# Revit family: KEUCO_14975010000
name_source: partatom
category: Allgemeines Modell
revit_build: Autodesk Revit 2016 (Build: 20150220_1215(x64)
units: mm (PartAtom-declared; Revit-internal decimal feet)

## family parameters
Arbeitsebenenbasiert = Ja
Beim Laden mit Abzugskörper schneiden = Nein
Bemaßung runder Anschluss = Durchmesser verwenden
Gemeinsam genutzt = Nein
Immer vertikal = Nein
Kann Basisbauteil für Bewehrung sein = Nein
Raumberechnungspunkt = Nein
Teiletyp = Normal

## types (3) — shared parameters
Beschreibung = mit Ablage aus ESG-Glas
Gewicht = 1.46
Hersteller = KEUCO
Kategorie = ACC
Länge = 600 mm  [stored 1.9685 ft]
Material Regal = Glas, weiß, hohe Luminanz
Serie = Plan
Tiefe = 235 mm  [stored 0.770997 ft]
URL = https://www.keuco.com
Verwendung = GWC / WP
Vorgabe-Ansicht = 1219 mm

## per-type parameters (varying)
| type | Ausschreibungstext | Rahmen Material |
| 14975010000 | KEUCO PLAN Handtuchablage, 14975010000
Handtuchablage aus transparentem ESG, Stärke 8 mm, 
Gesamtbreite 600 mm,
in ästhetischem, funktionalem Design, 
Handtuchhalter aus hochglanzverchromten Messingrohr, 
Durchmesser 25 mm,
leicht zu reinigen, antistatisch, Ausladung Handtuchhalter 112 mm,
Gesamthöhe 112 mm, Gesamtbreite 600 mm, Ausladung 235 mm,
die Handtuchablage wird verdeckt angebracht,
Lieferung inkl. korrosionsfreiem Befestigungsmaterial | Verchromt |
| 14975070000 | KEUCO PLAN Handtuchablage, 14975070000
Handtuchablage aus transparentem ESG, Stärke 8 mm, 
Gesamtbreite 600 mm,
in ästhetischem, funktionalem Design, 
Handtuchhalter aus hochwertigem Edelstahl, 
Durchmesser 25 mm,
leicht zu reinigen, antistatisch, Ausladung Handtuchhalter 112 mm,
Gesamthöhe 112 mm, Gesamtbreite 600 mm, Ausladung 235 mm,
die Handtuchablage wird verdeckt angebracht,
Lieferung inkl. korrosionsfreiem Befestigungsmaterial | Edelstahl |
| 14975170000 | KEUCO PLAN Handtuchablage, 14975170000
Handtuchablage aus transparentem ESG, Stärke 8 mm, 
Gesamtbreite 600 mm,
in ästhetischem, funktionalem Design, 
Handtuchhalter aus silber-exloxiertem Aluminiumrohr, 
Durchmesser 25 mm,
die Glasaufnahmen sind als Design-Element hochglanzverchromt,
leicht zu reinigen, antistatisch, Ausladung Handtuchhalter 112 mm,
Gesamthöhe 112 mm, Gesamtbreite 600 mm, Ausladung 235 mm,
die Handtuchablage wird verdeckt angebracht,
Lieferung inkl. korrosionsfreiem Befestigungsmaterial | Edelstahl |

note: column(s) folded — value = type name in every type: Artikelnummer

note: [stored X ft] marks values corroborated as IEEE doubles in the binary element streams (Revit-internal decimal feet)

## geometry (parser evidence)
native form markers: Blend x2, Sweep x3
no freeform markers — native parametric forms only
